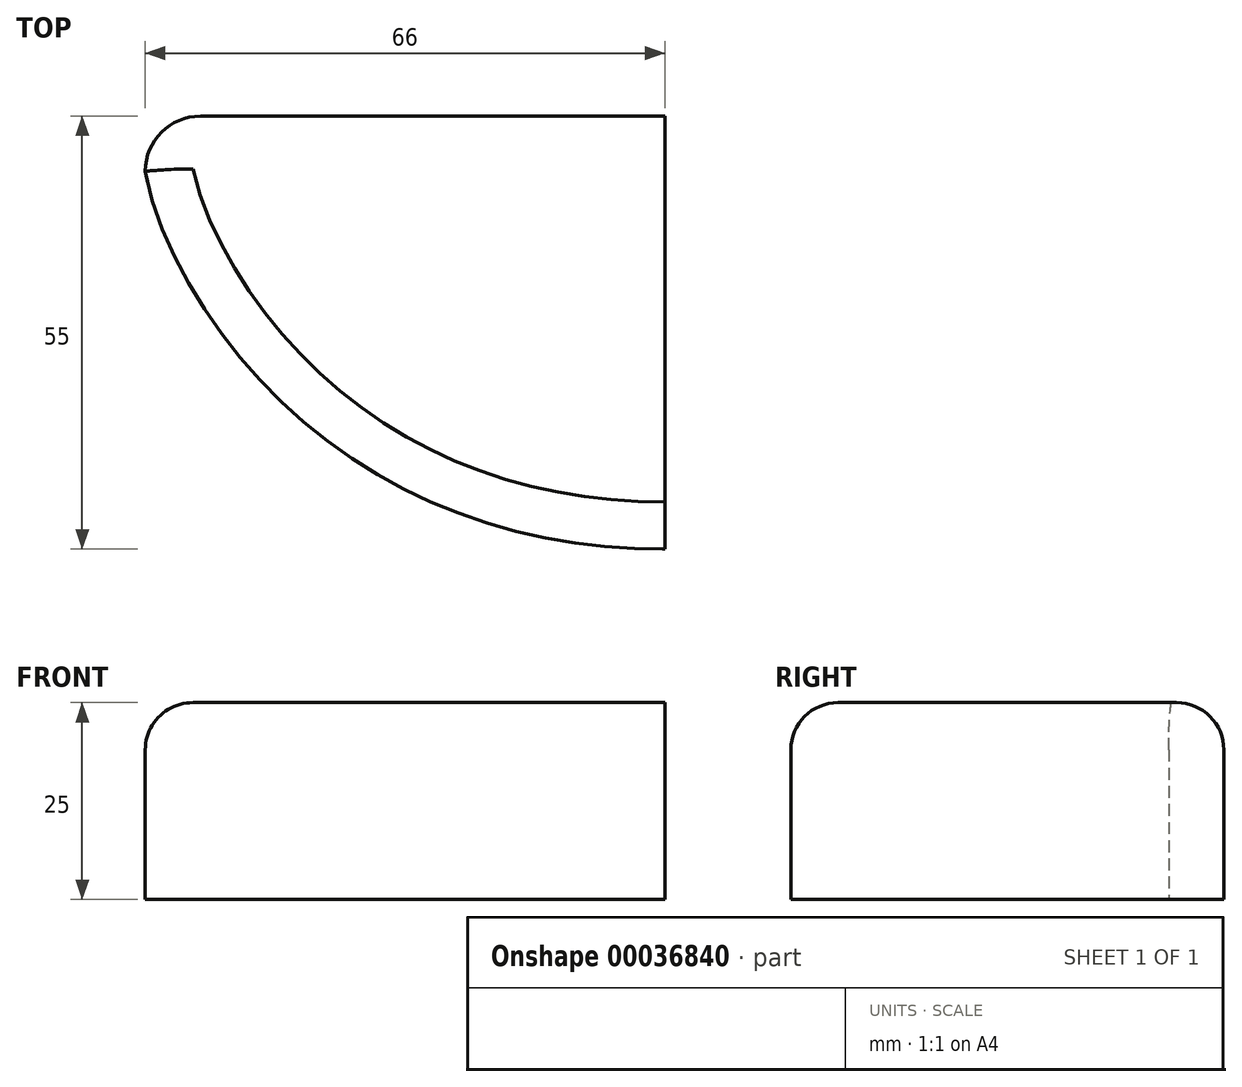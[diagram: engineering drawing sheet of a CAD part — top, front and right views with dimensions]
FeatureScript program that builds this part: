
annotation { "Feature Type Name" : "Feature", "Feature Type Description" : "" }
export const myFeature = defineFeature(function(context is Context, id is Id, definition is map)
    precondition{}
    {
        {
            var Q0;
            Q0=qCreatedBy(makeId("Top.planeOp"),FACE);
            var sketch = newSketch(context, id + "F0", { "sketchPlane" : qUnion([Q0])});
            skLineSegment(sketch, "E0.bottom", {"start": v(0, 19.18) * mm, "end": v(-59, 19.18) * mm});
            skLineSegment(sketch, "E0.top", {"start": v(0, -35.82) * mm, "end": v(-41, -35.82) * mm});
            skLineSegment(sketch, "E0.left", {"start": v(0, 19.18) * mm, "end": v(0, -35.82) * mm});
            skPoint(sketch, "E1.visualSharp", {"position": v(-66, 19.18) * mm});
            skArc(sketch, "E1.filletArc", {"start": v(-59, 19.18) * mm, "mid": v(-63.95, 17.13) * mm, "end": v(-66, 12.18) * mm});
            skLineSegment(sketch, "E2.left", {"start": v(0, -35.85) * mm, "end": v(0, -18.35) * mm});
            skLineSegment(sketch, "E2.right", {"start": v(-41, -35.85) * mm, "end": v(-41, -35.82) * mm});
            skFitSpline(sketch, "E3", {"points": [v(-66, 12.18) * mm, v(0, -35.82) * mm], "startDerivative": vector(6.23, -40.1) * mm, "endDerivative": vector(134.17, 0) * mm});
            skLineSegment(sketch, "E4", {"start": v(0, 19.18) * mm, "end": v(0, -18.35) * mm});
            skPoint(sketch, "E5.orphan", {"position": v(-66, -35.82) * mm});
            skPoint(sketch, "E6.trimOffspring.end.orphan", {"position": v(-41, -18.35) * mm});
            skSolve(sketch);
        }
        {
            var Q0;
            Q0=makeQuery(id+"F0.imprint","IMPRINT",FACE,{"disambiguationData":[TD([[makeQuery(id+"F0.imprint","IMPRINT",EDGE,{"derivedFrom":sQuery(id+"F0.wireOp",EDGE,"E0.bottom")}),1.0]])]});
            extrude(context, id + "F1", {"entities" : qUnion([Q0]), "depth" : 25 * mm});
        }
        {
            var Q0;
            Q0=makeQuery(id+"F1.opExtrude","CAP_EDGE",EDGE,{"disambiguationData":[OSD([sQuery(id+"F0.wireOp",EDGE,"E3")])],"isStart":false});
            var Q1;
            Q1=makeQuery(id+"F1.opExtrude","CAP_EDGE",EDGE,{"disambiguationData":[OSD([sQuery(id+"F0.wireOp",EDGE,"E1.filletArc")])],"isStart":false});
            var Q2;
            Q2=makeQuery(id+"F1.opExtrude","CAP_EDGE",EDGE,{"disambiguationData":[OSD([sQuery(id+"F0.wireOp",EDGE,"E0.bottom")])],"isStart":false});
            fillet(context, id + "F2", {"entities" : qUnion([Q0, Q1, Q2]), "radius" : 6 * mm, "tangentPropagation" : true, "allowEdgeOverflow" : false});
        }
    });
